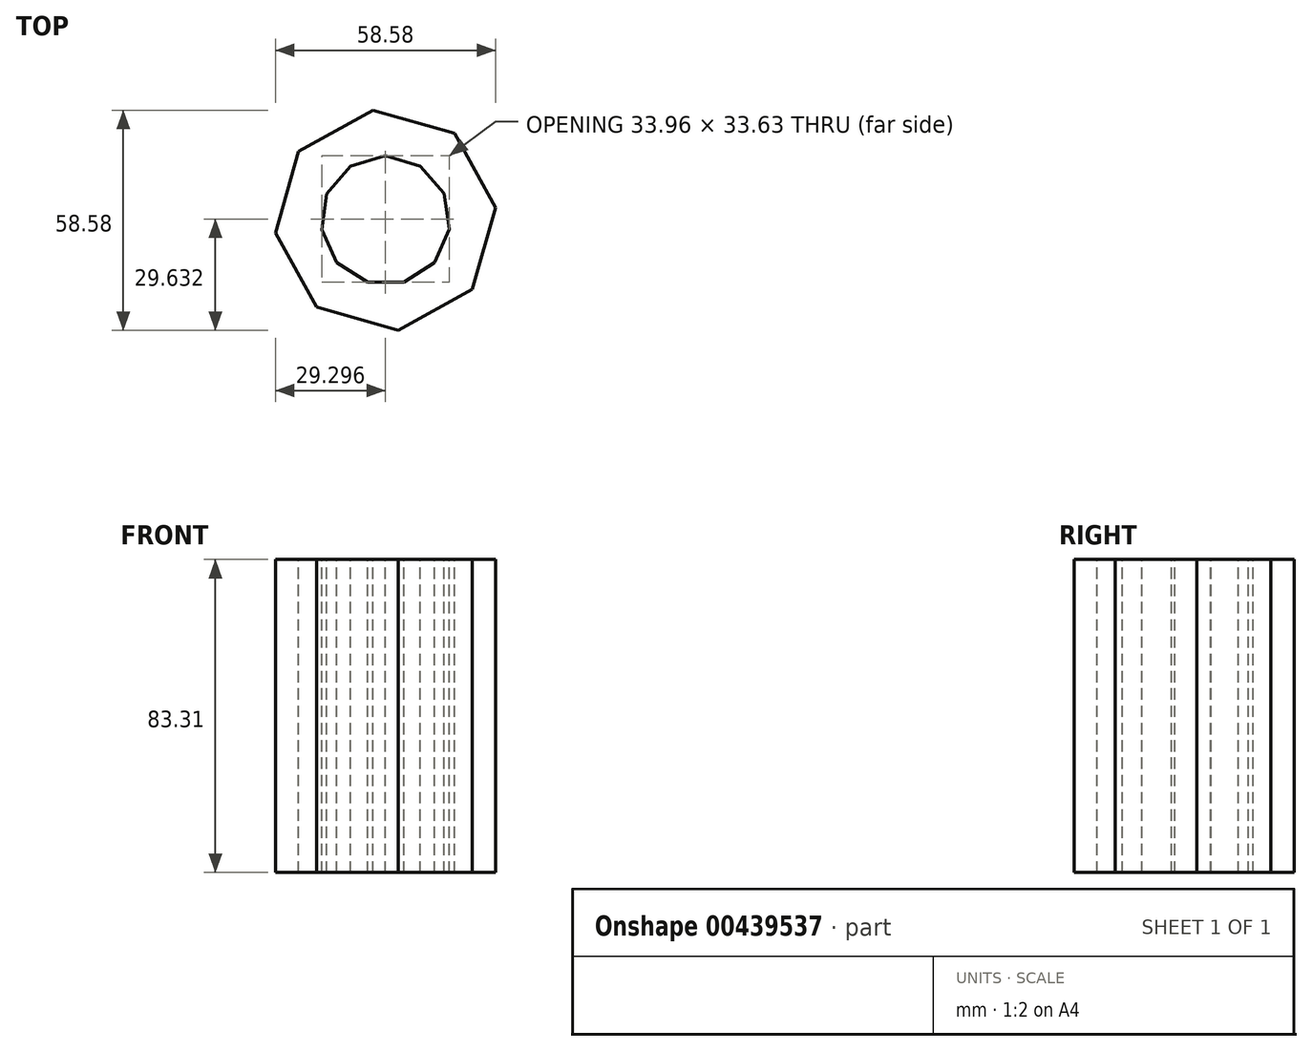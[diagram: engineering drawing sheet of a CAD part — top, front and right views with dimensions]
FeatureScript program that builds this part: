
annotation { "Feature Type Name" : "Feature", "Feature Type Description" : "" }
export const myFeature = defineFeature(function(context is Context, id is Id, definition is map)
    precondition{}
    {
        {
            var Q0;
            Q0=qCreatedBy(makeId("Top.planeOp"),FACE);
            var sketch = newSketch(context, id + "F0", { "sketchPlane" : qUnion([Q0])});
            skCircle(sketch, "E0.cCircle", {"center": v(0, 0) * mm, "radius": 29.48 * mm, "construction": true});
            skLineSegment(sketch, "E0.0", {"start": v(23.1, -18.32) * mm, "end": v(3.39, -29.29) * mm});
            skLineSegment(sketch, "E0.1", {"start": v(3.39, -29.29) * mm, "end": v(-18.32, -23.1) * mm});
            skLineSegment(sketch, "E0.2", {"start": v(-18.32, -23.1) * mm, "end": v(-29.29, -3.39) * mm});
            skLineSegment(sketch, "E0.3", {"start": v(-29.29, -3.39) * mm, "end": v(-23.1, 18.32) * mm});
            skLineSegment(sketch, "E0.4", {"start": v(-23.1, 18.32) * mm, "end": v(-3.39, 29.29) * mm});
            skLineSegment(sketch, "E0.5", {"start": v(-3.39, 29.29) * mm, "end": v(18.32, 23.1) * mm});
            skLineSegment(sketch, "E0.6", {"start": v(18.32, 23.1) * mm, "end": v(29.29, 3.39) * mm});
            skLineSegment(sketch, "E0.7", {"start": v(29.29, 3.39) * mm, "end": v(23.1, -18.32) * mm});
            skCircle(sketch, "E1.cCircle", {"center": v(0, 0) * mm, "radius": 17.16 * mm, "construction": true});
            skLineSegment(sketch, "E1.0", {"start": v(-9.3, 14.41) * mm, "end": v(-0.04, 17.16) * mm});
            skLineSegment(sketch, "E1.1", {"start": v(-0.04, 17.16) * mm, "end": v(9.24, 14.45) * mm});
            skLineSegment(sketch, "E1.2", {"start": v(9.24, 14.45) * mm, "end": v(15.59, 7.16) * mm});
            skLineSegment(sketch, "E1.3", {"start": v(15.59, 7.16) * mm, "end": v(16.99, -2.4) * mm});
            skLineSegment(sketch, "E1.4", {"start": v(16.99, -2.4) * mm, "end": v(13, -11.2) * mm});
            skLineSegment(sketch, "E1.5", {"start": v(13, -11.2) * mm, "end": v(4.87, -16.45) * mm});
            skLineSegment(sketch, "E1.6", {"start": v(4.87, -16.45) * mm, "end": v(-4.8, -16.47) * mm});
            skLineSegment(sketch, "E1.7", {"start": v(-4.8, -16.47) * mm, "end": v(-12.94, -11.27) * mm});
            skLineSegment(sketch, "E1.8", {"start": v(-12.94, -11.27) * mm, "end": v(-16.98, -2.48) * mm});
            skLineSegment(sketch, "E1.9", {"start": v(-16.98, -2.48) * mm, "end": v(-15.62, 7.09) * mm});
            skLineSegment(sketch, "E1.10", {"start": v(-15.62, 7.09) * mm, "end": v(-9.3, 14.41) * mm});
            skSolve(sketch);
        }
        {
            var Q0;
            Q0=makeQuery(id+"F0.imprint","IMPRINT",FACE,{"disambiguationData":[TD([[makeQuery(id+"F0.imprint","IMPRINT",EDGE,{"derivedFrom":sQuery(id+"F0.wireOp",EDGE,"E0.0")}),-1.0]])]});
            extrude(context, id + "F1", {"entities" : qUnion([Q0]), "oppositeDirection" : true, "depth" : 83.31 * mm});
        }
    });
